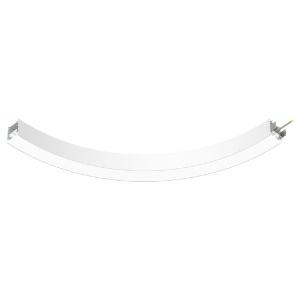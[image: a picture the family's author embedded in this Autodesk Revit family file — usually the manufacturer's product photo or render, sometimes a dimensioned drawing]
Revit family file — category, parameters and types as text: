
# Revit family: super-g_slim_super_g_slim_dir_ind_1550_90deg_hl_ps_led_36w__5760lm__3000k__cri80_430-3770_06a3
name_source: partatom
category: Leuchten
revit_build: Autodesk Revit 2016 (Build: 20190508_0715(x64)
units: mm (PartAtom-declared; Revit-internal decimal feet)

## family parameters
Basisbauteil = Fläche
Beim Laden mit Abzugskörper schneiden = Nein
Bemaßung runder Anschluss = Durchmesser verwenden
Gemeinsam genutzt = Nein
Lichtquelle = Nein
Raumberechnungspunkt = Nein
Teiletyp = Normal

## types (1)
- 430-3770-D01 (1 x LED, 720 lm, 3000K)
    Beschreibung = The insert consists of aluminum-extruded profile. Charming SOFT-EDGE design ensure unparalleled styling. The ballast is integrated and allows for an operation with 220-240V (50/60Hz). SUPER-G (# 430-3770) ist not dimmable (on/off).
    CIE Flux Codes = 48 79 96 66 85
    Color Rendering = 1B/80…89
    Color Temperature = 3000K
    Height = 90 mm
    Hersteller = Prolicht
    Lamp Light Flux = 720 lm
    Lamp count = 1
    Lampe = 1 x LED
    Length = 146 mm
    Luminous efficacy = 122 lm/W
    ModVariant = Nein
    Modell = 430-3770
    Mounting Place = Ceiling
    Mounting Type = Pendant
    Number of Poles = 1
    OnlyDefault = Ja
    Power Factor = 1
    Product Name = SUPER-G SLIM__SUPER G SLIM DIR/IND 1550/90° HL PS LED 36W  5760lm  3000K  CRI80
    Product group = Suspended profile systems
    ProductGroupID = 944
    Protection Class = Protection class
    Protection Degree = Degree of protection
    RLX_Detail_Level = 1
    RlxData = <blob elided: 31329 chars, md5=b59aad58>
    Scheinlast = 40 VA
    Socket = socket
    Standby Power = 0 W
    System Light Flux = 4873 lm
    System Power = 40 W
    Typenbild = 430-3770.jpg
    URL = http://relux.com
    VarID = 430-3770-d01
    Voltage = 0 V
    Vorgabe-Ansicht = 1800 mm
    Weight = 0.00 kg
    Width = 65 mm

## geometry (parser evidence)
native form markers: Blend x4, Sweep x47
no freeform markers — native parametric forms only
